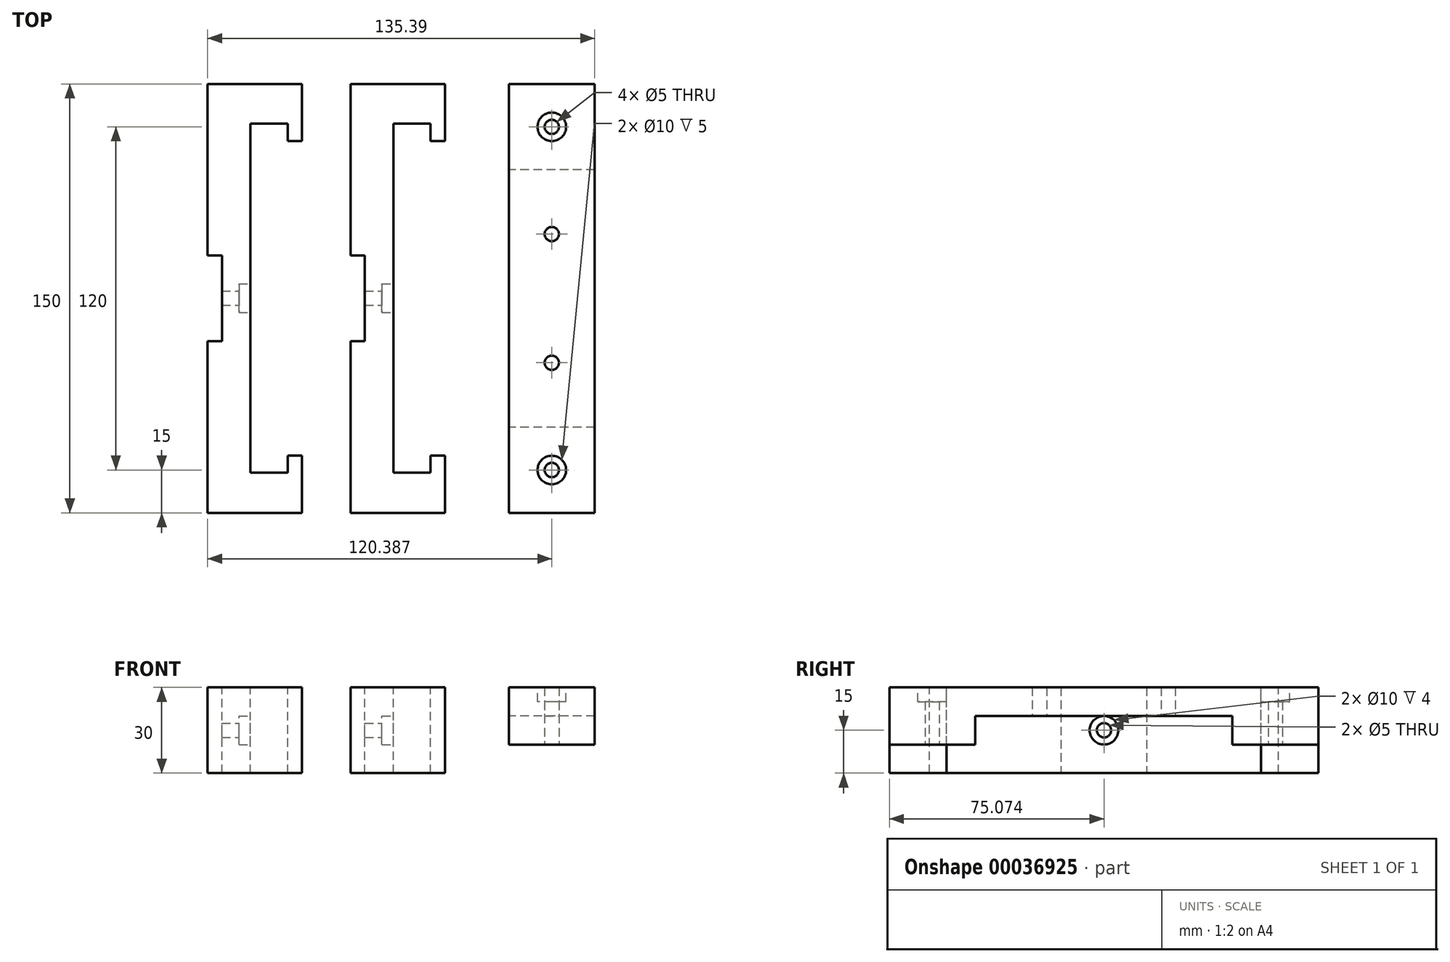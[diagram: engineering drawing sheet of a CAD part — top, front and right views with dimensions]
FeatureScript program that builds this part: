
annotation { "Feature Type Name" : "Feature", "Feature Type Description" : "" }
export const myFeature = defineFeature(function(context is Context, id is Id, definition is map)
    precondition{}
    {
        {
            var Q0;
            Q0=qCreatedBy(makeId("Top.planeOp"),FACE);
            var sketch = newSketch(context, id + "F0", { "sketchPlane" : qUnion([Q0])});
            skLineSegment(sketch, "E0.rect.bottom", {"start": v(70, -75) * mm, "end": v(-70, -75) * mm, "construction": true});
            skLineSegment(sketch, "E0.rect.top", {"start": v(70, 75) * mm, "end": v(-70, 75) * mm, "construction": true});
            skLineSegment(sketch, "E0.rect.left", {"start": v(70, -75) * mm, "end": v(70, 75) * mm, "construction": true});
            skLineSegment(sketch, "E0.rect.right", {"start": v(-70, -75) * mm, "end": v(-70, 75) * mm, "construction": true});
            skPoint(sketch, "E0.rect.middle", {"position": v(0, 0) * mm});
            skLineSegment(sketch, "E1.bottom", {"start": v(-70, 75) * mm, "end": v(-37, 75) * mm});
            skLineSegment(sketch, "E1.top", {"start": v(-70, -75) * mm, "end": v(-37, -75) * mm});
            skLineSegment(sketch, "E1.left", {"start": v(-70, 75) * mm, "end": v(-70, -75) * mm});
            skLineSegment(sketch, "E1.right", {"start": v(-37, 75) * mm, "end": v(-37, -75) * mm});
            skLineSegment(sketch, "E2", {"start": v(-70, 75) * mm, "end": v(-37, -75) * mm, "construction": true});
            skLineSegment(sketch, "E3", {"start": v(-37, 75) * mm, "end": v(-70, -75) * mm, "construction": true});
            skPoint(sketch, "E4", {"position": v(-53.5, 0) * mm});
            skLineSegment(sketch, "E5", {"start": v(-39.83, 75) * mm, "end": v(-39.83, 60) * mm, "construction": true});
            skLineSegment(sketch, "E6", {"start": v(-37, 60) * mm, "end": v(-42, 60) * mm, "construction": true});
            skLineSegment(sketch, "E7.bottom", {"start": v(-42, 60) * mm, "end": v(-37, 60) * mm, "construction": true});
            skLineSegment(sketch, "E7.right", {"start": v(-37, 60) * mm, "end": v(-37, 65) * mm, "construction": true});
            skLineSegment(sketch, "E8", {"start": v(-45.81, -75) * mm, "end": v(-45.81, -60) * mm, "construction": true});
            skLineSegment(sketch, "E9", {"start": v(-37, -60) * mm, "end": v(-42, -60) * mm, "construction": true});
            skLineSegment(sketch, "E10.right", {"start": v(-37, -60) * mm, "end": v(-37, -65) * mm, "construction": true});
            skLineSegment(sketch, "E11", {"start": v(-70, 0) * mm, "end": v(-55, 0) * mm, "construction": true});
            skPoint(sketch, "E11.endSnap0", {"position": v(-70, 0) * mm});
            skLineSegment(sketch, "E12", {"start": v(-37, 60) * mm, "end": v(-37, -60) * mm});
            skLineSegment(sketch, "E13.top", {"start": v(-37, 55) * mm, "end": v(-42, 55) * mm, "construction": true});
            skLineSegment(sketch, "E13.left", {"start": v(-37, 60) * mm, "end": v(-37, 55) * mm, "construction": true});
            skLineSegment(sketch, "E13.right", {"start": v(-42, 60) * mm, "end": v(-42, 55) * mm, "construction": true});
            skLineSegment(sketch, "E14.top", {"start": v(-37, -55) * mm, "end": v(-42, -55) * mm, "construction": true});
            skLineSegment(sketch, "E14.left", {"start": v(-37, -60) * mm, "end": v(-37, -55) * mm, "construction": true});
            skLineSegment(sketch, "E14.right", {"start": v(-42, -60) * mm, "end": v(-42, -55) * mm, "construction": true});
            skLineSegment(sketch, "E15.bottom", {"start": v(-42, 61.07) * mm, "end": v(-55, 61.07) * mm});
            skLineSegment(sketch, "E15.top", {"start": v(-42, -60.95) * mm, "end": v(-55, -60.95) * mm});
            skLineSegment(sketch, "E15.right", {"start": v(-55, 61.07) * mm, "end": v(-55, -60.95) * mm});
            skLineSegment(sketch, "E16", {"start": v(-42, 61.07) * mm, "end": v(-42, 55) * mm});
            skLineSegment(sketch, "E17", {"start": v(-42, 55) * mm, "end": v(-37, 55) * mm});
            skLineSegment(sketch, "E18", {"start": v(-37, 55) * mm, "end": v(-37, -55) * mm});
            skLineSegment(sketch, "E19", {"start": v(-37, -55) * mm, "end": v(-42, -55) * mm});
            skLineSegment(sketch, "E20", {"start": v(-42, -55) * mm, "end": v(-42, -60.95) * mm});
            skSolve(sketch);
        }
        {
            var Q0;
            {var subQ5=sQuery(id+"F0.wireOp",EDGE,"E1.bottom");Q0=makeQuery(id+"F0.imprint","IMPRINT",FACE,{"disambiguationData":[TD([[makeQuery(id+"F0.imprint","IMPRINT",EDGE,{"derivedFrom":subQ5}),-1.0]])]});}
            extrude(context, id + "F1", {"entities" : qUnion([Q0]), "oppositeDirection" : true, "depth" : 30 * mm});
        }
        {
            var Q0;
            Q0=makeQuery(id+"F1.opExtrude","CAP_FACE",FACE,{"disambiguationData":[OSD([sQuery(id+"F0.wireOp",EDGE,"E1.bottom"),sQuery(id+"F0.wireOp",EDGE,"E1.top"),sQuery(id+"F0.wireOp",EDGE,"E1.left"),sQuery(id+"F0.wireOp",EDGE,"E1.right"),sQuery(id+"F0.wireOp",EDGE,"73a533ee-4e9b-4bd2-b7d4-9101c5a2c7ed.bottom"),sQuery(id+"F0.wireOp",EDGE,"73a533ee-4e9b-4bd2-b7d4-9101c5a2c7ed.top"),sQuery(id+"F0.wireOp",EDGE,"73a533ee-4e9b-4bd2-b7d4-9101c5a2c7ed.right"),sQuery(id+"F0.wireOp",EDGE,"38ecc1d0-31c9-4565-a05b-09df5e9a350a"),sQuery(id+"F0.wireOp",EDGE,"15cff29f-d361-4bc8-bf2a-33eb6b65abd0"),sQuery(id+"F0.wireOp",EDGE,"30e5f908-2a54-4e08-86a1-49416832641a"),sQuery(id+"F0.wireOp",EDGE,"f80f57d4-a314-4025-9ff7-c073914416dd")])],"isStart":true});
            var sketch = newSketch(context, id + "F2", { "sketchPlane" : qUnion([Q0])});
            skLineSegment(sketch, "E21.rect.bottom", {"start": v(-65, -15) * mm, "end": v(-75, -15) * mm});
            skLineSegment(sketch, "E21.rect.top", {"start": v(-65, 15) * mm, "end": v(-75, 15) * mm});
            skLineSegment(sketch, "E21.rect.left", {"start": v(-65, -15) * mm, "end": v(-65, 15) * mm});
            skLineSegment(sketch, "E21.rect.right", {"start": v(-75, -15) * mm, "end": v(-75, 15) * mm});
            skPoint(sketch, "E21.rect.middle", {"position": v(-70, 0) * mm});
            skSolve(sketch);
        }
        {
            var Q0;
            Q0 = qSketchRegion(id + "F2", true);
            extrude(context, id + "F3", {"entities" : qUnion([Q0]), "operationType" : NewBodyOperationType.REMOVE, "oppositeDirection" : true, "depth" : 30 * mm});
        }
        {
            var Q0;
            Q0=makeQuery(id+"F1.opExtrude","SWEPT_FACE",FACE,{"disambiguationData":[OSD([sQuery(id+"F0.wireOp",EDGE,"E15.right")])]});
            var sketch = newSketch(context, id + "F4", { "sketchPlane" : qUnion([Q0])});
            skLineSegment(sketch, "E22.bottom", {"start": v(15.06, 0) * mm, "end": v(-14.9, 0) * mm, "construction": true});
            skLineSegment(sketch, "E22.top", {"start": v(15.06, -30) * mm, "end": v(-14.9, -30) * mm, "construction": true});
            skLineSegment(sketch, "E22.left", {"start": v(15.06, 0) * mm, "end": v(15.06, -30) * mm, "construction": true});
            skLineSegment(sketch, "E22.right", {"start": v(-14.9, 0) * mm, "end": v(-14.9, -30) * mm, "construction": true});
            skLineSegment(sketch, "E23", {"start": v(15.06, 0) * mm, "end": v(-14.9, -30) * mm, "construction": true});
            skLineSegment(sketch, "E24", {"start": v(15.06, -30) * mm, "end": v(-14.9, 0) * mm, "construction": true});
            skPoint(sketch, "E25", {"position": v(0.07, -15) * mm});
            skCircle(sketch, "E26", {"center": v(0.07, -15) * mm, "radius": 5 * mm});
            skSolve(sketch);
        }
        {
            var Q0;
            Q0 = qSketchRegion(id + "F4", true);
            extrude(context, id + "F5", {"entities" : qUnion([Q0]), "operationType" : NewBodyOperationType.REMOVE, "oppositeDirection" : true, "depth" : 4 * mm});
        }
        {
            var Q0;
            Q0=makeQuery(id+"F5.boolean.opBoolean","COPY",FACE,{"derivedFrom":makeQuery(id+"F5.opExtrude","CAP_FACE",FACE,{"disambiguationData":[OSD([sQuery(id+"F4.wireOp",EDGE,"E26")])],"isStart":false})});
            var sketch = newSketch(context, id + "F6", { "sketchPlane" : qUnion([Q0])});
            skCircle(sketch, "E27", {"center": v(0.07, -15) * mm, "radius": 2.5 * mm});
            skSolve(sketch);
        }
        {
            var Q0;
            Q0 = qSketchRegion(id + "F6", true);
            extrude(context, id + "F7", {"entities" : qUnion([Q0]), "operationType" : NewBodyOperationType.REMOVE, "oppositeDirection" : true, "depth" : 10 * mm});
        }
        {
            var Q0;
            Q0=makeQuery(id+"F1.opExtrude","SWEPT_BODY",BODY,{"disambiguationData":[OSD([sQuery(id+"F0.wireOp",EDGE,"E1.bottom"),sQuery(id+"F0.wireOp",EDGE,"E1.top"),sQuery(id+"F0.wireOp",EDGE,"E1.left"),sQuery(id+"F0.wireOp",EDGE,"E1.right"),sQuery(id+"F0.wireOp",EDGE,"E12"),sQuery(id+"F0.wireOp",EDGE,"E15.bottom"),sQuery(id+"F0.wireOp",EDGE,"E15.top"),sQuery(id+"F0.wireOp",EDGE,"E15.right"),sQuery(id+"F0.wireOp",EDGE,"E16"),sQuery(id+"F0.wireOp",EDGE,"E17"),sQuery(id+"F0.wireOp",EDGE,"E19"),sQuery(id+"F0.wireOp",EDGE,"E20")])]});
            transform(context, id + "F8", {"entities" : qUnion([Q0]), "transformType" : TransformType.TRANSLATION_3D, "dx" : 50 * mm, "dy" : 0 * mm, "dz" : 0 * mm, "makeCopy" : true});
        }
        {
            var Q0;
            Q0=qCreatedBy(makeId("Top.planeOp"),FACE);
            var sketch = newSketch(context, id + "F9", { "sketchPlane" : qUnion([Q0])});
            skLineSegment(sketch, "E28.rect.bottom", {"start": v(65.39, -75) * mm, "end": v(35.39, -75) * mm});
            skLineSegment(sketch, "E28.rect.top", {"start": v(65.39, 75) * mm, "end": v(35.39, 75) * mm});
            skLineSegment(sketch, "E28.rect.left", {"start": v(65.39, -75) * mm, "end": v(65.39, 75) * mm});
            skLineSegment(sketch, "E28.rect.right", {"start": v(35.39, -75) * mm, "end": v(35.39, 75) * mm});
            skPoint(sketch, "E28.rect.middle", {"position": v(50.39, 0) * mm});
            skSolve(sketch);
        }
        {
            var Q0;
            Q0 = qSketchRegion(id + "F9", true);
            extrude(context, id + "F10", {"entities" : qUnion([Q0]), "oppositeDirection" : true, "depth" : 10 * mm});
        }
        {
            var Q0;
            Q0=makeQuery(id+"F10.opExtrude","CAP_FACE",FACE,{"disambiguationData":[OSD([sQuery(id+"F9.wireOp",EDGE,"E28.rect.bottom"),sQuery(id+"F9.wireOp",EDGE,"E28.rect.top"),sQuery(id+"F9.wireOp",EDGE,"E28.rect.left"),sQuery(id+"F9.wireOp",EDGE,"E28.rect.right")])],"isStart":false});
            var sketch = newSketch(context, id + "F11", { "sketchPlane" : qUnion([Q0])});
            skLineSegment(sketch, "E29.bottom", {"start": v(65.39, -75) * mm, "end": v(35.39, -75) * mm});
            skLineSegment(sketch, "E29.top", {"start": v(65.39, -45) * mm, "end": v(35.39, -45) * mm});
            skLineSegment(sketch, "E29.left", {"start": v(65.39, -75) * mm, "end": v(65.39, -45) * mm});
            skLineSegment(sketch, "E29.right", {"start": v(35.39, -75) * mm, "end": v(35.39, -45) * mm});
            skLineSegment(sketch, "E30.bottom", {"start": v(65.39, 75) * mm, "end": v(35.39, 75) * mm});
            skLineSegment(sketch, "E30.top", {"start": v(65.39, 45) * mm, "end": v(35.39, 45) * mm});
            skLineSegment(sketch, "E30.left", {"start": v(65.39, 75) * mm, "end": v(65.39, 45) * mm});
            skLineSegment(sketch, "E30.right", {"start": v(35.39, 75) * mm, "end": v(35.39, 45) * mm});
            skSolve(sketch);
        }
        {
            var Q0;
            Q0 = qSketchRegion(id + "F11", true);
            extrude(context, id + "F12", {"entities" : qUnion([Q0]), "operationType" : NewBodyOperationType.ADD, "depth" : 10 * mm});
        }
        {
            var Q0;
            Q0=makeQuery(id+"F12.opExtrude","CAP_FACE",FACE,{"disambiguationData":[OSD([sQuery(id+"F11.wireOp",EDGE,"E29.bottom"),sQuery(id+"F11.wireOp",EDGE,"E29.top"),sQuery(id+"F11.wireOp",EDGE,"E29.left"),sQuery(id+"F11.wireOp",EDGE,"E29.right")])],"isStart":false});
            var sketch = newSketch(context, id + "F13", { "sketchPlane" : qUnion([Q0])});
            skLineSegment(sketch, "E31", {"start": v(65.39, -75) * mm, "end": v(35.39, -45) * mm, "construction": true});
            skLineSegment(sketch, "E32", {"start": v(65.39, -45) * mm, "end": v(35.39, -75) * mm, "construction": true});
            skPoint(sketch, "E33", {"position": v(50.39, -60) * mm});
            skCircle(sketch, "E34", {"center": v(50.39, -60) * mm, "radius": 2.5 * mm});
            skSolve(sketch);
        }
        {
            var Q0;
            Q0 = qSketchRegion(id + "F13", true);
            extrude(context, id + "F14", {"entities" : qUnion([Q0]), "operationType" : NewBodyOperationType.REMOVE, "oppositeDirection" : true, "depth" : 25 * mm});
        }
        {
            var Q0;
            Q0=makeQuery(id+"F12.opExtrude","CAP_FACE",FACE,{"disambiguationData":[OSD([sQuery(id+"F11.wireOp",EDGE,"E30.bottom"),sQuery(id+"F11.wireOp",EDGE,"E30.top"),sQuery(id+"F11.wireOp",EDGE,"E30.left"),sQuery(id+"F11.wireOp",EDGE,"E30.right")])],"isStart":false});
            var sketch = newSketch(context, id + "F15", { "sketchPlane" : qUnion([Q0])});
            skLineSegment(sketch, "E35", {"start": v(65.39, 45) * mm, "end": v(35.39, 75) * mm, "construction": true});
            skLineSegment(sketch, "E36", {"start": v(65.39, 75) * mm, "end": v(35.39, 45) * mm, "construction": true});
            skPoint(sketch, "E37", {"position": v(50.39, 60) * mm});
            skCircle(sketch, "E38", {"center": v(50.39, 60) * mm, "radius": 2.5 * mm});
            skSolve(sketch);
        }
        {
            var Q0;
            Q0 = qSketchRegion(id + "F15", true);
            extrude(context, id + "F16", {"entities" : qUnion([Q0]), "operationType" : NewBodyOperationType.REMOVE, "oppositeDirection" : true, "depth" : 25 * mm});
        }
        {
            var Q0;
            Q0=makeQuery(id+"F10.opExtrude","CAP_FACE",FACE,{"disambiguationData":[OSD([sQuery(id+"F9.wireOp",EDGE,"E28.rect.bottom"),sQuery(id+"F9.wireOp",EDGE,"E28.rect.top"),sQuery(id+"F9.wireOp",EDGE,"E28.rect.left"),sQuery(id+"F9.wireOp",EDGE,"E28.rect.right")])],"isStart":true});
            var sketch = newSketch(context, id + "F17", { "sketchPlane" : qUnion([Q0])});
            skCircle(sketch, "E39", {"center": v(50.39, 60) * mm, "radius": 5 * mm});
            skCircle(sketch, "E40", {"center": v(50.39, -60) * mm, "radius": 5 * mm});
            skSolve(sketch);
        }
        {
            var Q0;
            Q0 = qSketchRegion(id + "F17", true);
            extrude(context, id + "F18", {"entities" : qUnion([Q0]), "operationType" : NewBodyOperationType.REMOVE, "oppositeDirection" : true, "depth" : 5 * mm});
        }
        {
            var Q0;
            Q0=makeQuery(id+"F10.opExtrude","CAP_FACE",FACE,{"disambiguationData":[OSD([sQuery(id+"F9.wireOp",EDGE,"E28.rect.bottom"),sQuery(id+"F9.wireOp",EDGE,"E28.rect.top"),sQuery(id+"F9.wireOp",EDGE,"E28.rect.left"),sQuery(id+"F9.wireOp",EDGE,"E28.rect.right")])],"isStart":false});
            var sketch = newSketch(context, id + "F19", { "sketchPlane" : qUnion([Q0])});
            skLineSegment(sketch, "E41", {"start": v(65.39, -45) * mm, "end": v(35.39, 0) * mm, "construction": true});
            skLineSegment(sketch, "E42", {"start": v(35.39, -45) * mm, "end": v(65.39, 0) * mm, "construction": true});
            skLineSegment(sketch, "E43", {"start": v(65.39, 0) * mm, "end": v(35.39, 45) * mm, "construction": true});
            skLineSegment(sketch, "E44", {"start": v(65.39, 45) * mm, "end": v(35.39, 0) * mm, "construction": true});
            skPoint(sketch, "E45", {"position": v(50.39, -22.5) * mm});
            skPoint(sketch, "E46", {"position": v(50.39, 22.5) * mm});
            skCircle(sketch, "E47", {"center": v(50.39, -22.5) * mm, "radius": 2.5 * mm});
            skCircle(sketch, "E48", {"center": v(50.39, 22.5) * mm, "radius": 2.5 * mm});
            skSolve(sketch);
        }
        {
            var Q0;
            Q0 = qSketchRegion(id + "F19", true);
            extrude(context, id + "F20", {"entities" : qUnion([Q0]), "operationType" : NewBodyOperationType.REMOVE, "oppositeDirection" : true, "depth" : 10 * mm});
        }
    });
